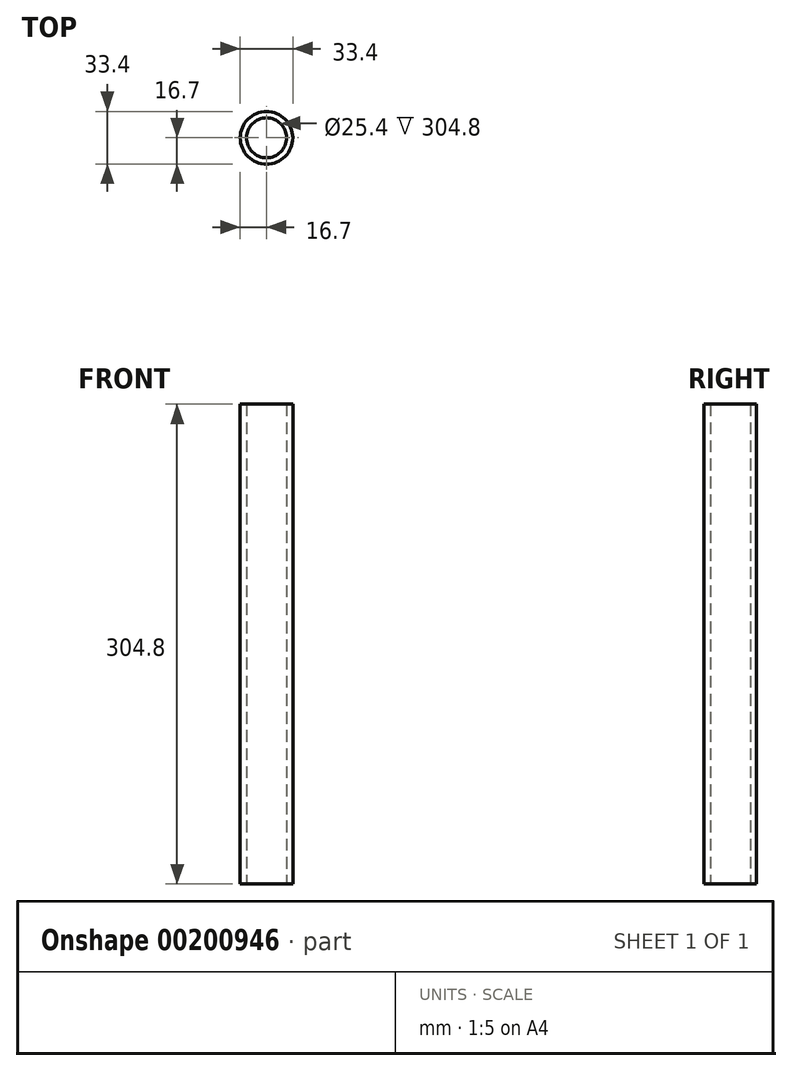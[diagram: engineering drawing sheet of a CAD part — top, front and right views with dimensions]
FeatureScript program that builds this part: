
annotation { "Feature Type Name" : "Feature", "Feature Type Description" : "" }
export const myFeature = defineFeature(function(context is Context, id is Id, definition is map)
    precondition{}
    {
        {
            var Q0;
            Q0=qCreatedBy(makeId("Top.planeOp"),FACE);
            var sketch = newSketch(context, id + "F0", { "sketchPlane" : qUnion([Q0])});
            skCircle(sketch, "E0", {"center": v(0, 0) * mm, "radius": 16.7 * mm});
            skCircle(sketch, "E1", {"center": v(0, 0) * mm, "radius": 12.7 * mm});
            skSolve(sketch);
        }
        {
            var Q0;
            Q0=makeQuery(id+"F0.imprint","IMPRINT",FACE,{"disambiguationData":[TD([[makeQuery(id+"F0.imprint","IMPRINT",EDGE,{"derivedFrom":sQuery(id+"F0.wireOp",EDGE,"E0")}),1.0]])]});
            extrude(context, id + "F1", {"entities" : qUnion([Q0]), "depth" : 304.8 * mm});
        }
    });
